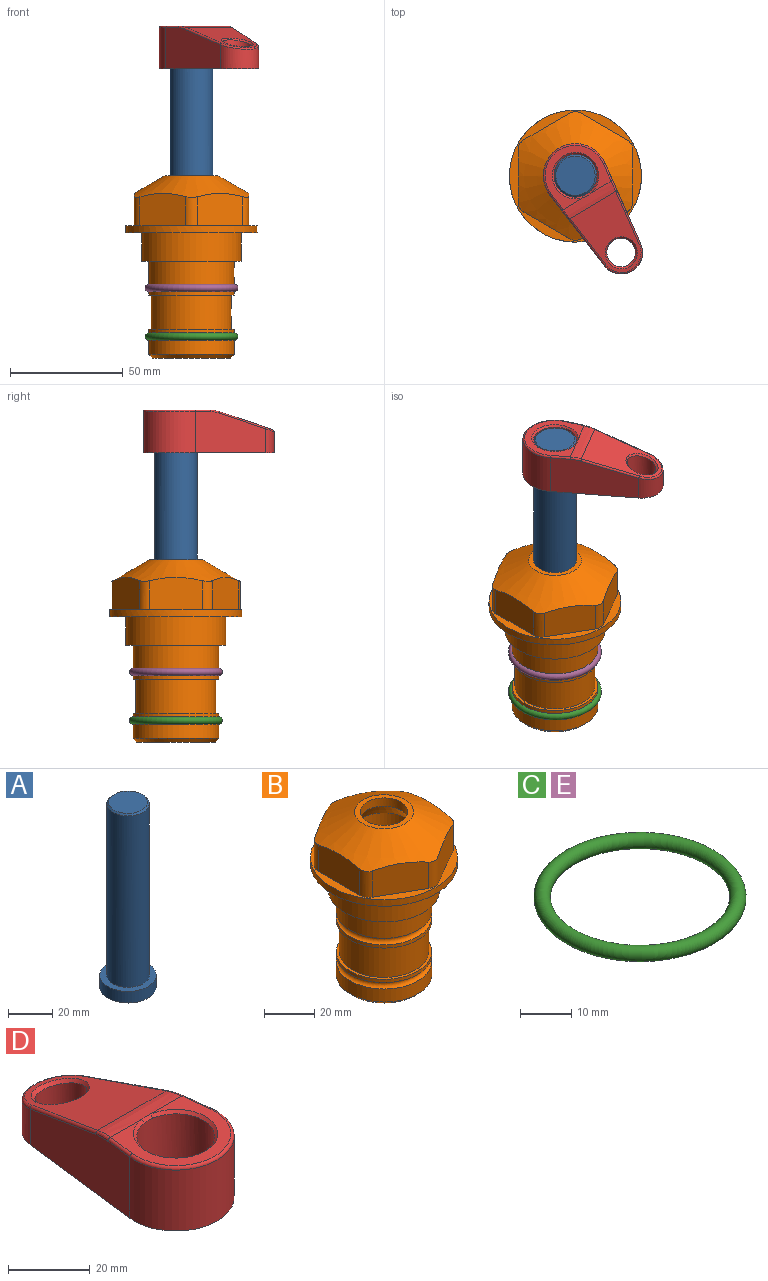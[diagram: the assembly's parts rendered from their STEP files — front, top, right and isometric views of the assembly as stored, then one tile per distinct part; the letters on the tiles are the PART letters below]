
ASSEMBLY  parts=5 mates=4
PART A: 6 faces, bbox 25.4x25.4x101.6 mm
  f0: plane 17.46x17.46mm, normal (0,0,1), area 239.5mm2, adj f5
  f1: plane 25.4x25.4mm, normal (0,0,-1), area 506.7mm2, adj f2
  f2: cylinder r=12.7mm len=25.4mm, axis (0,0,1), area 506.7mm2, adj f1,f3
  f3: plane 25.4x25.4mm, normal (0,0,1), area 221.7mm2, adj f2,f4
  f4: cylinder r=9.53mm len=94.46mm, axis (0,0,1), area 5653mm2, adj f3,f5
  f5: cone r=8.73mm half-angle=45deg, axis (0,0,-1), area 64.4mm2, adj f0,f4
PART B: 36 faces, bbox 58.7x58.7x81 mm
  f0: cylinder r=17.78mm len=35.56mm, axis (0,0,1), area 1670.8mm2, adj f23,f24,f31
  f1: cylinder r=19.05mm len=38.1mm, axis (0,0,1), area 1191.9mm2, adj f26,f27,f30
  f2: plane 58.66x58.66mm, normal (0,0,-1), area 1150.6mm2, adj f3,f28
  f3: cylinder r=29.33mm len=58.66mm, axis (0,0,-1), area 585.1mm2, adj f2,f4
  f4: plane 58.66x58.66mm, normal (0,0,1), area 475.9mm2, adj f3,f5,f6,f7,f8,f9,f10,f11
  f5: plane 20.32x14.34mm, normal (-0.5,0.87,0), area 324.4mm2, adj f4,f15,f16,f17
  f6: plane 20.32x14.34mm, normal (0.5,0.87,0), area 324.4mm2, adj f4,f14,f15,f17
  f7: plane 23.48x14.34mm, normal (1,0,0), area 324.4mm2, adj f4,f13,f14,f17
  f8: plane 20.32x14.34mm, normal (0.5,-0.87,0), area 324.4mm2, adj f4,f12,f13,f17
  f9: plane 20.32x14.34mm, normal (-0.5,-0.87,0), area 324.4mm2, adj f4,f11,f12,f17
  f10: plane 23.48x14.34mm, normal (-1,0,0), area 324.4mm2, adj f4,f11,f16,f17
  f11: cylinder r=5.08mm len=12.85mm, axis (0,0,-1), area 67.2mm2, adj f4,f9,f10,f17
  f12: cylinder r=5.08mm len=12.85mm, axis (0,0,-1), area 67.2mm2, adj f4,f8,f9,f17
  f13: cylinder r=5.08mm len=12.85mm, axis (0,0,-1), area 67.2mm2, adj f4,f7,f8,f17
  f14: cylinder r=5.08mm len=12.85mm, axis (0,0,-1), area 67.2mm2, adj f4,f6,f7,f17
  f15: cylinder r=5.08mm len=12.85mm, axis (0,0,-1), area 67.2mm2, adj f4,f5,f6,f17
  f16: cylinder r=5.08mm len=12.85mm, axis (0,0,-1), area 67.2mm2, adj f4,f5,f10,f17
  f17: cone r=11.73mm half-angle=60deg, axis (0,0,-1), area 2071.8mm2, adj f5,f6,f7,f8,f9,f10,f11,f12
  f18: plane 23.46x23.46mm, normal (0,0,1), area 147.4mm2, adj f17,f35
  f19: plane 34.93x34.93mm, normal (0,0,-1), area 958mm2, adj f29
  f20: cylinder r=19.05mm len=38.1mm, axis (0,0,1), area 760.1mm2, adj f21,f29
  f21: torus R=19.05mm, axis (0,0,1), area 565.3mm2, adj f20,f22
  f22: cylinder r=19.05mm len=38.1mm, axis (0,0,1), area 190mm2, adj f21,f23
  f23: plane 38.1x38.1mm, normal (0,0,1), area 146.9mm2, adj f0,f22
  f24: plane 38.1x38.1mm, normal (0,0,-1), area 146.9mm2, adj f0,f25
  f25: cylinder r=19.05mm len=38.1mm, axis (0,0,1), area 190mm2, adj f24,f26
  f26: torus R=19.05mm, axis (0,0,1), area 565.3mm2, adj f1,f25
  f27: plane 44.45x44.45mm, normal (0,0,-1), area 411.7mm2, adj f1,f28
  f28: cylinder r=22.23mm len=44.45mm, axis (0,0,1), area 1773.5mm2, adj f2,f27
  f29: cone r=19.05mm half-angle=45deg, axis (0,0,1), area 257.5mm2, adj f19,f20
  f30: cylinder r=3.17mm len=6.75mm, axis (-1,0,0), area 128mm2, adj f1,f33
  f31: cylinder r=3.17mm len=6.35mm, axis (-1,0,0), area 102.5mm2, adj f0,f33
  f32: plane 25.4x25.4mm, normal (0,0,1), area 506.7mm2, adj f33
  f33: cylinder r=12.7mm len=66.42mm, axis (0,0,-1), area 5236.2mm2, adj f30,f31,f32,f34
  f34: cone r=9.53mm half-angle=30deg, axis (0,0,-1), area 443.4mm2, adj f33,f35
  f35: cylinder r=9.53mm len=19.05mm, axis (0,0,-1), area 240.9mm2, adj f18,f34
PART C: 1 faces, bbox 44.7x44.7x3.2 mm
  f0: torus R=19.05mm, axis (0,0,1), area 1193.9mm2
PART D: 31 faces, bbox 31.7x65.5x19.8 mm
  f0: plane 39.12x18.26mm, normal (0.99,0.12,0), area 612.2mm2, adj f1,f4,f7,f11,f13,f15
  f1: cylinder r=9.53mm len=18.91mm, axis (0,0,-1), area 296.1mm2, adj f0,f2,f7,f17
  f2: plane 39.12x18.26mm, normal (-0.99,0.12,0), area 612.2mm2, adj f1,f4,f7,f12,f14,f16
  f3: cylinder r=6.35mm len=12.7mm, axis (0,0,-1), area 362.4mm2, adj f7,f18
  f4: cylinder r=14.29mm len=28.58mm, axis (0,0,-1), area 882.2mm2, adj f0,f2,f7,f10
  f5: cylinder r=9.53mm len=19.05mm, axis (0,0,-1), area 1092.6mm2, adj f7,f19,f20
  f6: plane 26.99x23.69mm, normal (0,0,1), area 216.2mm2, adj f9,f10,f11,f12,f19
  f7: plane 63.5x28.58mm, normal (0,0,-1), area 661.8mm2, adj f0,f1,f2,f3,f4,f5,f22,f23
  f8: plane 33.52x23.6mm, normal (0,0.26,0.97), area 486mm2, adj f9,f15,f16,f17,f18
  f9: cylinder r=19.05mm len=24.72mm, axis (1,0,0), area 120.4mm2, adj f6,f8,f13,f14,f20
  f10: torus R=13.49mm, axis (0,0,1), area 59mm2, adj f4,f6,f11,f12
  f11: cylinder r=0.79mm len=8.67mm, axis (0.12,-0.99,0), area 10.8mm2, adj f0,f6,f10,f13
  f12: cylinder r=0.79mm len=8.67mm, axis (0.12,0.99,0), area 10.8mm2, adj f2,f6,f10,f14
  f13: bspline ~4.95x1.42mm, area 6.1mm2, adj f0,f9,f11,f15
  f14: bspline ~4.95x1.42mm, area 6.1mm2, adj f2,f9,f12,f16
  f15: cylinder r=0.79mm len=25.95mm, axis (0.12,-0.96,0.26), area 32.9mm2, adj f0,f8,f13,f17
  f16: cylinder r=0.79mm len=25.95mm, axis (0.12,0.96,-0.26), area 32.9mm2, adj f2,f8,f14,f17
  f17: bspline ~18.91x8.38mm, area 30mm2, adj f1,f8,f15,f16
  f18: bspline ~14.29x14.29mm, area 48.3mm2, adj f3,f8
  f19: cone r=9.53mm half-angle=45deg, axis (0,0,1), area 66.5mm2, adj f5,f6,f20
  f20: bspline ~3.22x0.96mm, area 3.5mm2, adj f5,f9,f19
  f21: plane 2.75x2.72mm, normal (0,0,-1), area 2.9mm2, adj f23,f25,f28
  f22: plane 23.05x15.88mm, normal (-0.99,-0.12,0), area 323.6mm2, adj f7,f25,f26,f27,f28,f29
  f23: plane 23.05x15.88mm, normal (0.99,-0.12,0), area 323.6mm2, adj f7,f21,f25,f27,f28,f30
  f24: cylinder r=9.53mm len=10.69mm, axis (0,0,-1), area 114.7mm2, adj f7,f27,f29,f30
  f25: cylinder r=12.7mm len=20.59mm, axis (0,0,-1), area 381.1mm2, adj f7,f21,f22,f23,f26,f28
  f26: plane 2.75x2.72mm, normal (0,0,-1), area 2.9mm2, adj f22,f25,f28
  f27: plane 19.72x18.37mm, normal (0,-0.26,-0.97), area 291.8mm2, adj f22,f23,f24,f28,f29,f30
  f28: cylinder r=15.88mm len=19.92mm, axis (1,0,0), area 54.8mm2, adj f21,f22,f23,f25,f26,f27
  f29: cylinder r=1.59mm len=11mm, axis (0,0,-1), area 34.7mm2, adj f7,f22,f24,f27
  f30: cylinder r=1.59mm len=11mm, axis (0,0,-1), area 34.7mm2, adj f7,f23,f24,f27
PART E: same geometry as C
PLACE A rot(axis=(0,0,-1),149.3deg) t=(0,0,27.55)mm
PLACE B at identity fixed
PLACE C t=(0,0,-21.59)mm
PLACE D rot(axis=(0,0,-1),149.3deg) t=(0,0,28.35)mm
PLACE E at identity
MATE fastened C.f0 <-> B.f0  axis (0,0,1) through (0,0,-46.1)mm
MATE fastened E.f0 <-> B.f0  axis (0,0,1) through (0,0,-24.51)mm
MATE fastened A.f2 <-> D.f4  axis (0,0,1) through (0,0,91.05)mm
MATE cylindrical A.f2 <-> B.f0  axis (0,0,-1) through (0,0,-10.55)mm
